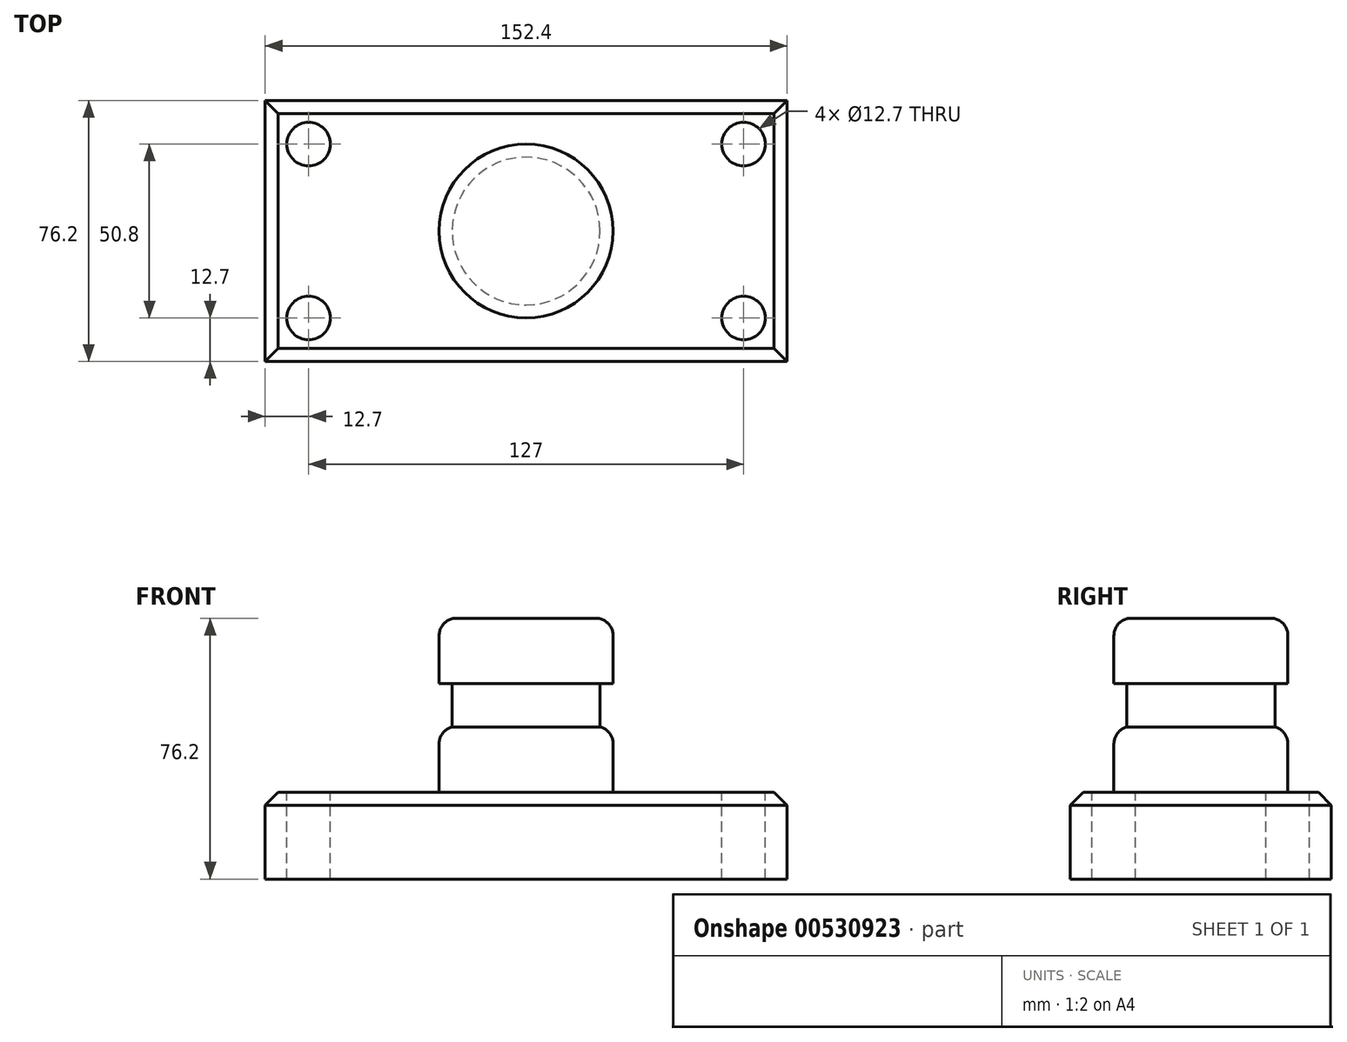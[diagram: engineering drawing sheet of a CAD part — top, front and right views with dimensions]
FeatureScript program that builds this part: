
annotation { "Feature Type Name" : "Feature", "Feature Type Description" : "" }
export const myFeature = defineFeature(function(context is Context, id is Id, definition is map)
    precondition{}
    {
        {
            var Q0;
            Q0=qCreatedBy(makeId("Top.planeOp"),FACE);
            var sketch = newSketch(context, id + "F0", { "sketchPlane" : qUnion([Q0])});
            skLineSegment(sketch, "E0.bottom", {"start": v(76.2, 38.1) * mm, "end": v(-76.2, 38.1) * mm});
            skLineSegment(sketch, "E0.top", {"start": v(76.2, -38.1) * mm, "end": v(-76.2, -38.1) * mm});
            skLineSegment(sketch, "E0.left", {"start": v(76.2, 38.1) * mm, "end": v(76.2, -38.1) * mm});
            skLineSegment(sketch, "E0.right", {"start": v(-76.2, 38.1) * mm, "end": v(-76.2, -38.1) * mm});
            skPoint(sketch, "E0.middle", {"position": v(0, 0) * mm});
            skSolve(sketch);
        }
        {
            var Q0;
            Q0=makeQuery(id+"F0.imprint","IMPRINT",FACE,{"disambiguationData":[TD([[makeQuery(id+"F0.imprint","IMPRINT",EDGE,{"derivedFrom":sQuery(id+"F0.wireOp",EDGE,"E0.bottom")}),1.0]])]});
            extrude(context, id + "F1", {"entities" : qUnion([Q0]), "depth" : 25.4 * mm, "offsetDistance" : 25.4 * mm});
        }
        {
            var Q0;
            Q0=makeQuery(id+"F1.opExtrude","CAP_FACE",FACE,{"disambiguationData":[OSD([sQuery(id+"F0.wireOp",EDGE,"E0.bottom"),sQuery(id+"F0.wireOp",EDGE,"E0.top"),sQuery(id+"F0.wireOp",EDGE,"E0.left"),sQuery(id+"F0.wireOp",EDGE,"E0.right")])],"isStart":false});
            var sketch = newSketch(context, id + "F2", { "sketchPlane" : qUnion([Q0])});
            skCircle(sketch, "E1", {"center": v(-63.5, 25.4) * mm, "radius": 6.35 * mm});
            skCircle(sketch, "E2", {"center": v(63.5, 25.4) * mm, "radius": 6.35 * mm});
            skCircle(sketch, "E3", {"center": v(-63.5, -25.4) * mm, "radius": 6.35 * mm});
            skCircle(sketch, "E4", {"center": v(63.5, -25.4) * mm, "radius": 6.35 * mm});
            skSolve(sketch);
        }
        {
            var Q0;
            Q0=makeQuery(id+"F2.imprint","IMPRINT",FACE,{"disambiguationData":[TD([[makeQuery(id+"F2.imprint","IMPRINT",EDGE,{"derivedFrom":sQuery(id+"F2.wireOp",EDGE,"E1")}),1.0]])]});
            var Q1;
            Q1=makeQuery(id+"F2.imprint","IMPRINT",FACE,{"disambiguationData":[TD([[makeQuery(id+"F2.imprint","IMPRINT",EDGE,{"derivedFrom":sQuery(id+"F2.wireOp",EDGE,"E2")}),1.0]])]});
            var Q2;
            Q2=makeQuery(id+"F2.imprint","IMPRINT",FACE,{"disambiguationData":[TD([[makeQuery(id+"F2.imprint","IMPRINT",EDGE,{"derivedFrom":sQuery(id+"F2.wireOp",EDGE,"E4")}),1.0]])]});
            var Q3;
            Q3=makeQuery(id+"F2.imprint","IMPRINT",FACE,{"disambiguationData":[TD([[makeQuery(id+"F2.imprint","IMPRINT",EDGE,{"derivedFrom":sQuery(id+"F2.wireOp",EDGE,"E3")}),1.0]])]});
            extrude(context, id + "F3", {"entities" : qUnion([Q0, Q1, Q2, Q3]), "operationType" : NewBodyOperationType.REMOVE, "endBound" : BoundingType.THROUGH_ALL, "oppositeDirection" : true, "depth" : 25.4 * mm, "offsetDistance" : 25.4 * mm});
        }
        {
            var Q0;
            Q0=makeQuery(id+"F1.opExtrude","CAP_EDGE",EDGE,{"disambiguationData":[OSD([sQuery(id+"F0.wireOp",EDGE,"E0.top")])],"isStart":false});
            var Q1;
            Q1=makeQuery(id+"F1.opExtrude","CAP_EDGE",EDGE,{"disambiguationData":[OSD([sQuery(id+"F0.wireOp",EDGE,"E0.right")])],"isStart":false});
            var Q2;
            Q2=makeQuery(id+"F1.opExtrude","CAP_EDGE",EDGE,{"disambiguationData":[OSD([sQuery(id+"F0.wireOp",EDGE,"E0.bottom")])],"isStart":false});
            var Q3;
            Q3=makeQuery(id+"F1.opExtrude","CAP_EDGE",EDGE,{"disambiguationData":[OSD([sQuery(id+"F0.wireOp",EDGE,"E0.left")])],"isStart":false});
            chamfer(context, id + "F4", {"entities" : qUnion([Q0, Q1, Q2, Q3]), "width" : 3.8 * mm, "tangentPropagation" : true});
        }
        {
            var Q0;
            Q0=qCreatedBy(makeId("Front.planeOp"),FACE);
            var sketch = newSketch(context, id + "F5", { "sketchPlane" : qUnion([Q0])});
            skLineSegment(sketch, "E5.bottom", {"start": v(0, 25.4) * mm, "end": v(25.4, 25.4) * mm});
            skLineSegment(sketch, "E5.top", {"start": v(0, 76.2) * mm, "end": v(25.4, 76.2) * mm});
            skLineSegment(sketch, "E5.left", {"start": v(0, 25.4) * mm, "end": v(0, 76.2) * mm});
            skLineSegment(sketch, "E5.right", {"start": v(25.4, 25.4) * mm, "end": v(25.4, 76.2) * mm});
            skLineSegment(sketch, "E6.bottom", {"start": v(25.4, 44.45) * mm, "end": v(21.59, 44.45) * mm});
            skLineSegment(sketch, "E6.top", {"start": v(25.4, 57.15) * mm, "end": v(21.59, 57.15) * mm});
            skLineSegment(sketch, "E6.left", {"start": v(25.4, 44.45) * mm, "end": v(25.4, 57.15) * mm});
            skLineSegment(sketch, "E6.right", {"start": v(21.59, 44.45) * mm, "end": v(21.59, 57.15) * mm});
            skSolve(sketch);
        }
        {
            var Q0;
            {var subQ4=sQuery(id+"F5.wireOp",EDGE,"E5.bottom");Q0=makeQuery(id+"F5.imprint","IMPRINT",FACE,{"disambiguationData":[TD([[makeQuery(id+"F5.imprint","IMPRINT",EDGE,{"derivedFrom":subQ4}),1.0]])]});}
            var Q1;
            Q1=sQuery(id+"F5.wireOp",EDGE,"E5.left");
            revolve(context, id + "F6", {"operationType" : NewBodyOperationType.ADD, "entities" : qUnion([Q0]), "axis" : qUnion([Q1]), "revolveType" : RevolveType.FULL});
        }
        {
            var Q0;
            Q0=makeQuery(id+"F6.opRevolve","SWEPT_EDGE",EDGE,{"disambiguationData":[OSD([sQuery(id+"F5.wireOp",EDGE,"E5.bottom"),sQuery(id+"F5.wireOp",EDGE,"E5.right")])]});
            var Q1;
            Q1=makeQuery(id+"F6.opRevolve","SWEPT_EDGE",EDGE,{"disambiguationData":[OSD([sQuery(id+"F5.wireOp",EDGE,"E5.right"),sQuery(id+"F5.wireOp",EDGE,"E6.bottom"),sQuery(id+"F5.wireOp",EDGE,"E6.left")])]});
            var Q2;
            Q2=makeQuery(id+"F6.opRevolve","SWEPT_EDGE",EDGE,{"disambiguationData":[OSD([sQuery(id+"F5.wireOp",EDGE,"E5.top"),sQuery(id+"F5.wireOp",EDGE,"E5.right")])]});
            fillet(context, id + "F7", {"entities" : qUnion([Q0, Q1, Q2]), "radius" : 5.08 * mm, "tangentPropagation" : true, "allowEdgeOverflow" : false});
        }
    });
